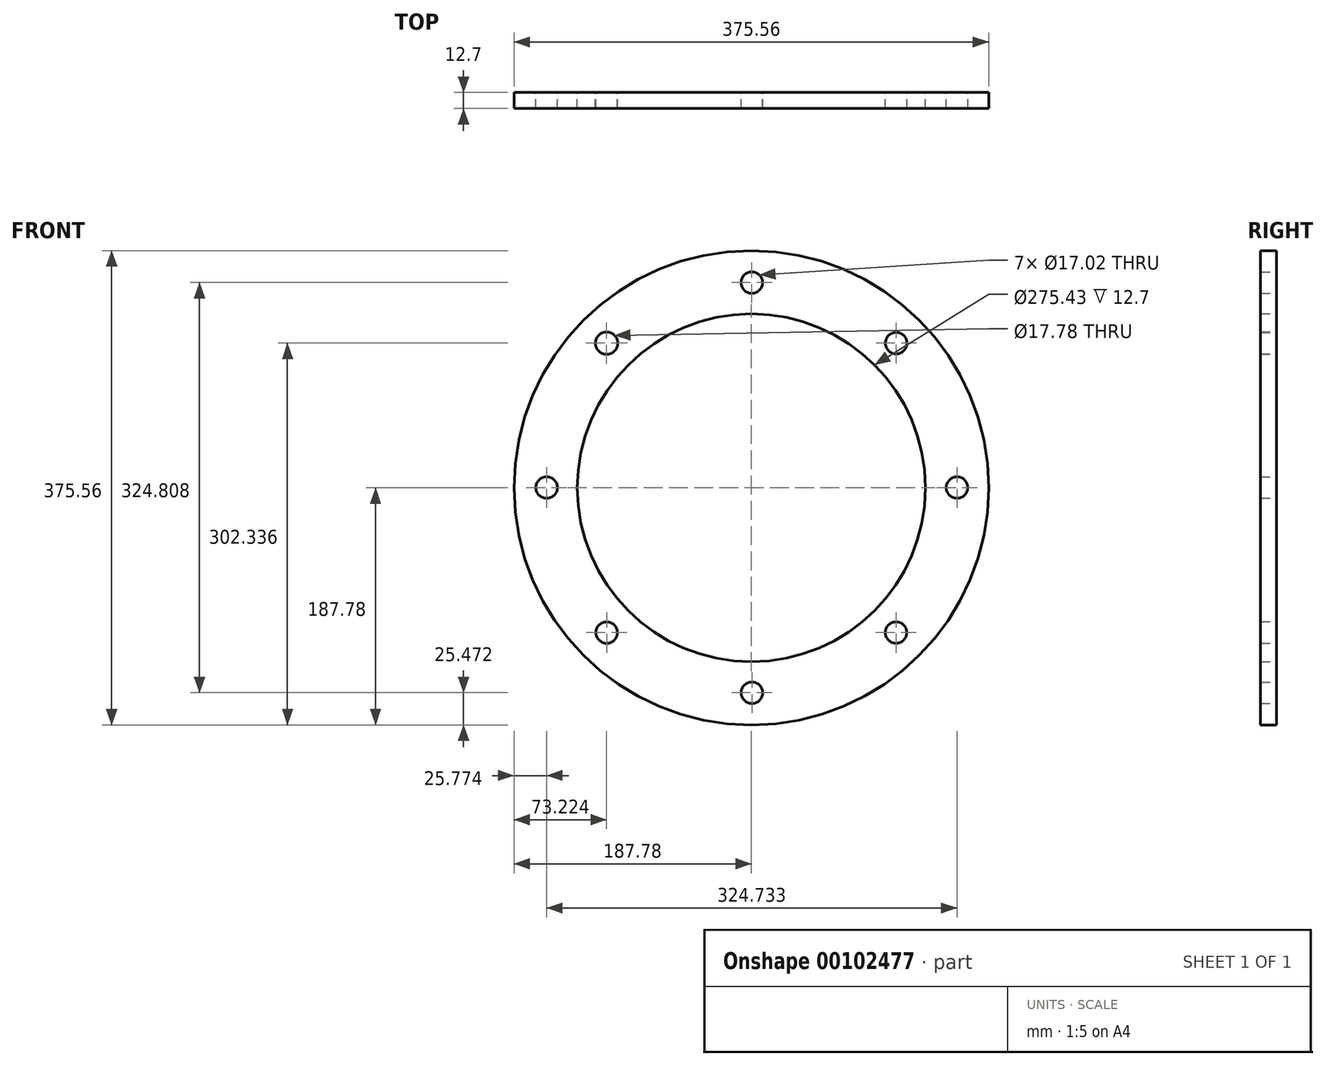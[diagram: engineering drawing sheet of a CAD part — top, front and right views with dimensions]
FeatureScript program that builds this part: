
annotation { "Feature Type Name" : "Feature", "Feature Type Description" : "" }
export const myFeature = defineFeature(function(context is Context, id is Id, definition is map)
    precondition{}
    {
        {
            var Q0;
            Q0=qCreatedBy(makeId("Front.planeOp"),FACE);
            var sketch = newSketch(context, id + "F0", { "sketchPlane" : qUnion([Q0])});
            skCircle(sketch, "E0", {"center": v(-114.56, 114.56) * mm, "radius": 8.9 * mm});
            skCircle(sketch, "E1", {"center": v(0.39, 162.5) * mm, "radius": 8.5 * mm});
            skCircle(sketch, "E2", {"center": v(114.6, 114.6) * mm, "radius": 8.5 * mm});
            skCircle(sketch, "E3", {"center": v(-162, 0.17) * mm, "radius": 8.5 * mm});
            skCircle(sketch, "E4", {"center": v(162.73, 0.17) * mm, "radius": 8.5 * mm});
            skCircle(sketch, "E5", {"center": v(-114.48, -114.63) * mm, "radius": 8.5 * mm});
            skCircle(sketch, "E6", {"center": v(0.47, -162.3) * mm, "radius": 8.5 * mm});
            skCircle(sketch, "E7", {"center": v(114.5, -114.62) * mm, "radius": 8.5 * mm});
            skCircle(sketch, "E8", {"center": v(0, 0) * mm, "radius": 187.78 * mm});
            skCircle(sketch, "E9", {"center": v(0, 0) * mm, "radius": 137.72 * mm});
            skSolve(sketch);
        }
        {
            var Q0;
            Q0 = qSketchRegion(id + "F0", true);
            extrude(context, id + "F1", {"entities" : qUnion([Q0]), "depth" : 12.7 * mm});
        }
    });
